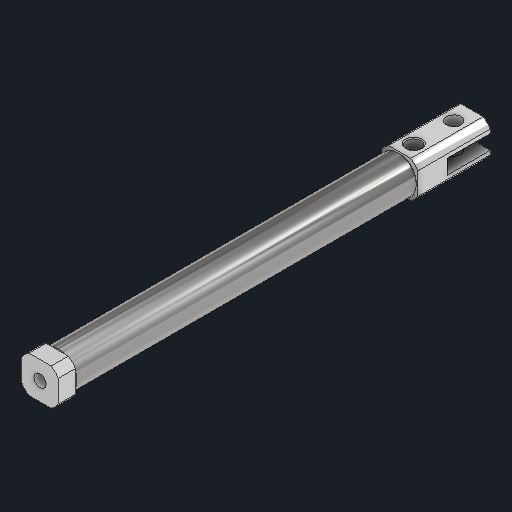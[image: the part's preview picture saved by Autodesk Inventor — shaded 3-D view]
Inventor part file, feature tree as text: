
AUTODESK INVENTOR PART (.ipt)
format: ipt  version: 2024 (Build 280153000, 153)  size: 187,904 bytes
history: native  units: in
note: dims shown in document units (in); Inventor stores cm internally (conversion verified against a paired STEP export)
features: extrude x1, thread x1, other x1
ambient origin geometry x8: Origin, YZ Plane, XZ Plane, XY Plane, X Axis, Y Axis, Z Axis, Center Point
bodies: Solid1 (feature_tree)
feature tree (3):
  extrude  "Extrusion3"  TaperAngle=0.0deg  [1 undecoded]
  thread  "Thread1"  [1 undecoded]
  other  "D-ClevisPinDetail"
note: 2 required parameter values undecoded (feature->parameter linkage not recoverable at this tier; creation-order binding heuristic only, values carry confidence <= 0.55)
